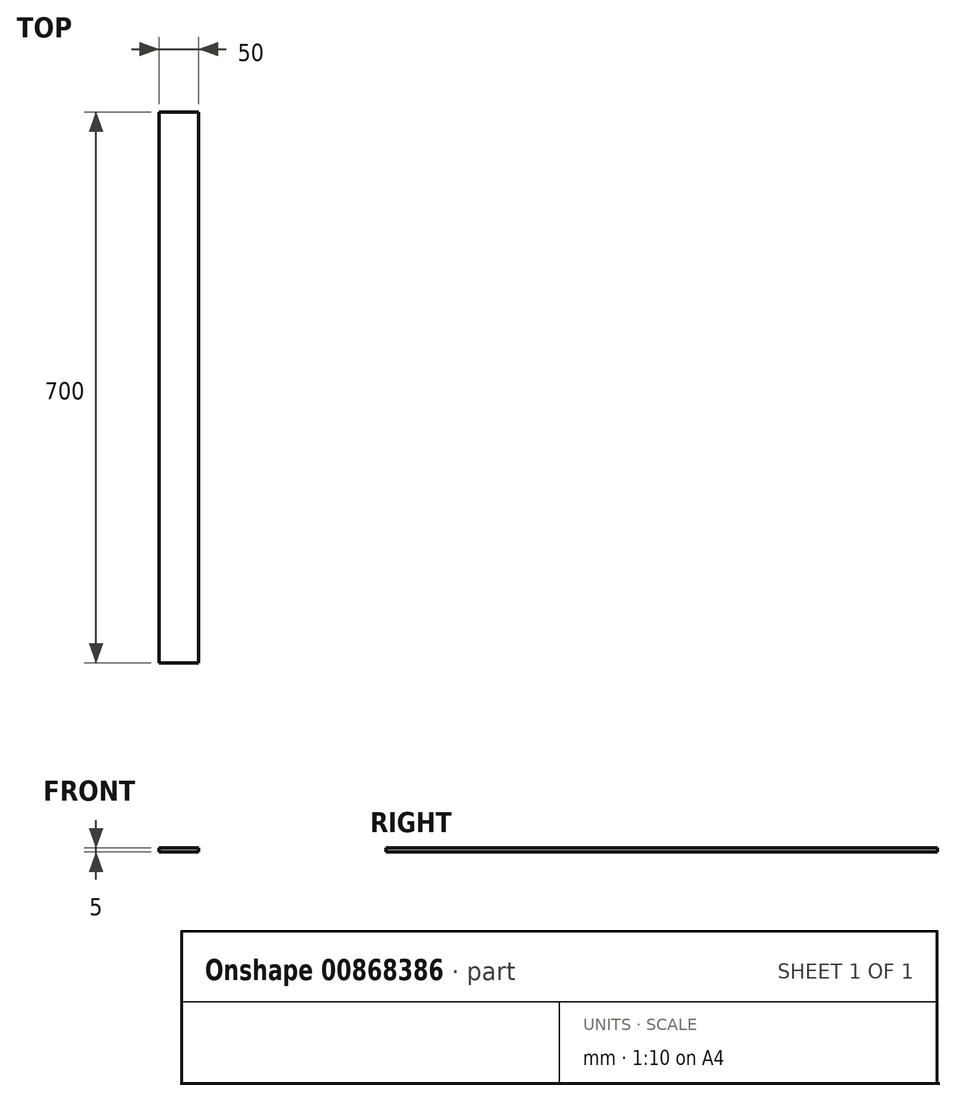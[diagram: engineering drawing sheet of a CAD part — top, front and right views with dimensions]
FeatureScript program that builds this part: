
annotation { "Feature Type Name" : "Feature", "Feature Type Description" : "" }
export const myFeature = defineFeature(function(context is Context, id is Id, definition is map)
    precondition{}
    {
        {
            var Q0;
            Q0=qCreatedBy(makeId("Top.planeOp"),FACE);
            var sketch = newSketch(context, id + "F0", { "sketchPlane" : qUnion([Q0])});
            skLineSegment(sketch, "E0.bottom", {"start": v(0, 0) * mm, "end": v(-50, 0) * mm});
            skLineSegment(sketch, "E0.top", {"start": v(0, 700) * mm, "end": v(-50, 700) * mm});
            skLineSegment(sketch, "E0.left", {"start": v(0, 0) * mm, "end": v(0, 700) * mm});
            skLineSegment(sketch, "E0.right", {"start": v(-50, 0) * mm, "end": v(-50, 700) * mm});
            skSolve(sketch);
        }
        {
            var Q0;
            Q0 = qSketchRegion(id + "F0", true);
            extrude(context, id + "F1", {"entities" : qUnion([Q0]), "depth" : 5 * mm, "offsetDistance" : 25 * mm});
        }
    });
